# Revit family: DLH-Series Bar Joist
name_source: partatom
category: Structural Framing
revit_build: Autodesk Revit Architecture 2012 (Build: 20110210_1515)
units: mm (PartAtom-declared; Revit-internal decimal feet)

## types (42) — shared parameters
Assembly Code = B1010350
Chord Thickness = 0' - 0 1/2"
Cord Leg = 0' - 2 1/2"
Rendering Material = <By Category>
Seat Depth = 0' - 5"
Seat Length = 0' - 6"
Vertical Member Visibility = Yes
Web Thickness = 0' - 1"

## per-type parameters (varying)
| type | Depth | End Panel | Wt |
| 52DLH10 | 4' - 4" | 6' - 6" | 25 |
| 52DLH11 | 4' - 4" | 6' - 6" | 26 |
| 52DLH12 | 4' - 4" | 6' - 6" | 29 |
| 52DLH13 | 4' - 4" | 6' - 6" | 34 |
| 52DLH14 | 4' - 4" | 6' - 6" | 39 |
| 52DLH15 | 4' - 4" | 6' - 6" | 42 |
| 52DLH16 | 4' - 4" | 6' - 6" | 45 |
| 52DLH17 | 4' - 4" | 6' - 6" | 52 |
| 56DLH11 | 4' - 8" | 7' - 0" | 26 |
| 56DLH12 | 4' - 8" | 7' - 0" | 30 |
| 56DLH13 | 4' - 8" | 7' - 0" | 34 |
| 56DLH14 | 4' - 8" | 7' - 0" | 39 |
| 56DLH15 | 4' - 8" | 7' - 0" | 42 |
| 56DLH16 | 4' - 8" | 7' - 0" | 46 |
| 56DLH17 | 4' - 8" | 7' - 0" | 51 |
| 60DLH12 | 5' - 0" | 7' - 6" | 29 |
| 60DLH13 | 5' - 0" | 7' - 6" | 35 |
| 60DLH14 | 5' - 0" | 7' - 6" | 40 |
| 60DLH15 | 5' - 0" | 7' - 6" | 43 |
| 60DLH16 | 5' - 0" | 7' - 6" | 46 |
| 60DLH17 | 5' - 0" | 7' - 6" | 52 |
| 60DLH18 | 5' - 0" | 7' - 6" | 59 |
| 64DLH12 | 5' - 4" | 8' - 0" | 31 |
| 64DLH13 | 5' - 4" | 8' - 0" | 34 |
| 64DLH14 | 5' - 4" | 8' - 0" | 40 |
| 64DLH15 | 5' - 4" | 8' - 0" | 43 |
| 64DLH16 | 5' - 4" | 8' - 0" | 46 |
| 64DLH17 | 5' - 4" | 8' - 0" | 52 |
| 64DLH18 | 5' - 4" | 8' - 0" | 59 |
| 68DLH13 | 5' - 8" | 8' - 6" | 37 |
| 68DLH14 | 5' - 8" | 8' - 6" | 40 |
| 68DLH15 | 5' - 8" | 8' - 6" | 44 |
| 68DLH16 | 5' - 8" | 8' - 6" | 49 |
| 68DLH17 | 5' - 8" | 8' - 6" | 55 |
| 68DLH18 | 5' - 8" | 8' - 6" | 61 |
| 68DLH19 | 5' - 8" | 8' - 6" | 67 |
| 72DLH14 | 6' - 0" | 9' - 0" | 41 |
| 72DLH15 | 6' - 0" | 9' - 0" | 44 |
| 72DLH16 | 6' - 0" | 9' - 0" | 50 |
| 72DLH17 | 6' - 0" | 9' - 0" | 56 |
| 72DLH18 | 6' - 0" | 9' - 0" | 59 |
| 72DLH19 | 6' - 0" | 9' - 0" | 70 |

## geometry (parser evidence)
native form markers: Sweep x8
no freeform markers — native parametric forms only
